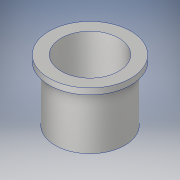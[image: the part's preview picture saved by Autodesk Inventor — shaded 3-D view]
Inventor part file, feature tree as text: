
AUTODESK INVENTOR PART (.ipt)
format: ipt  version: 2017 (Build 210142000, 142)  size: 142,848 bytes
history: native  units: in
note: dims shown in document units (in); Inventor stores cm internally (conversion verified against a paired STEP export)
features: revolve x1, sketch x1
ambient origin geometry x8: Origin, YZ Plane, XZ Plane, XY Plane, X Axis, Y Axis, Z Axis, Center Point
bodies: Body1 (feature_tree)
feature tree (2):
  revolve  "Revolution2"  [1 undecoded]
  sketch  "Sketch1"  dims[d0=0.25in d1=0.1718in d2=15.0deg d4=0.25in d5=1.5in d6=1.25in d7=0.25in d11=0.25in d13=0.5in d15=0.25in d16=0.25in d18=0.125in d19=0.5in d20=0.125in d21=0.25in d22=0.125in d23=0.125in d24=0.25in d25=0.5in d26=2.292in d27=0.5in d29=90.0deg]
note: 1 required parameter value undecoded (feature->parameter linkage not recoverable at this tier; creation-order binding heuristic only, values carry confidence <= 0.55)
